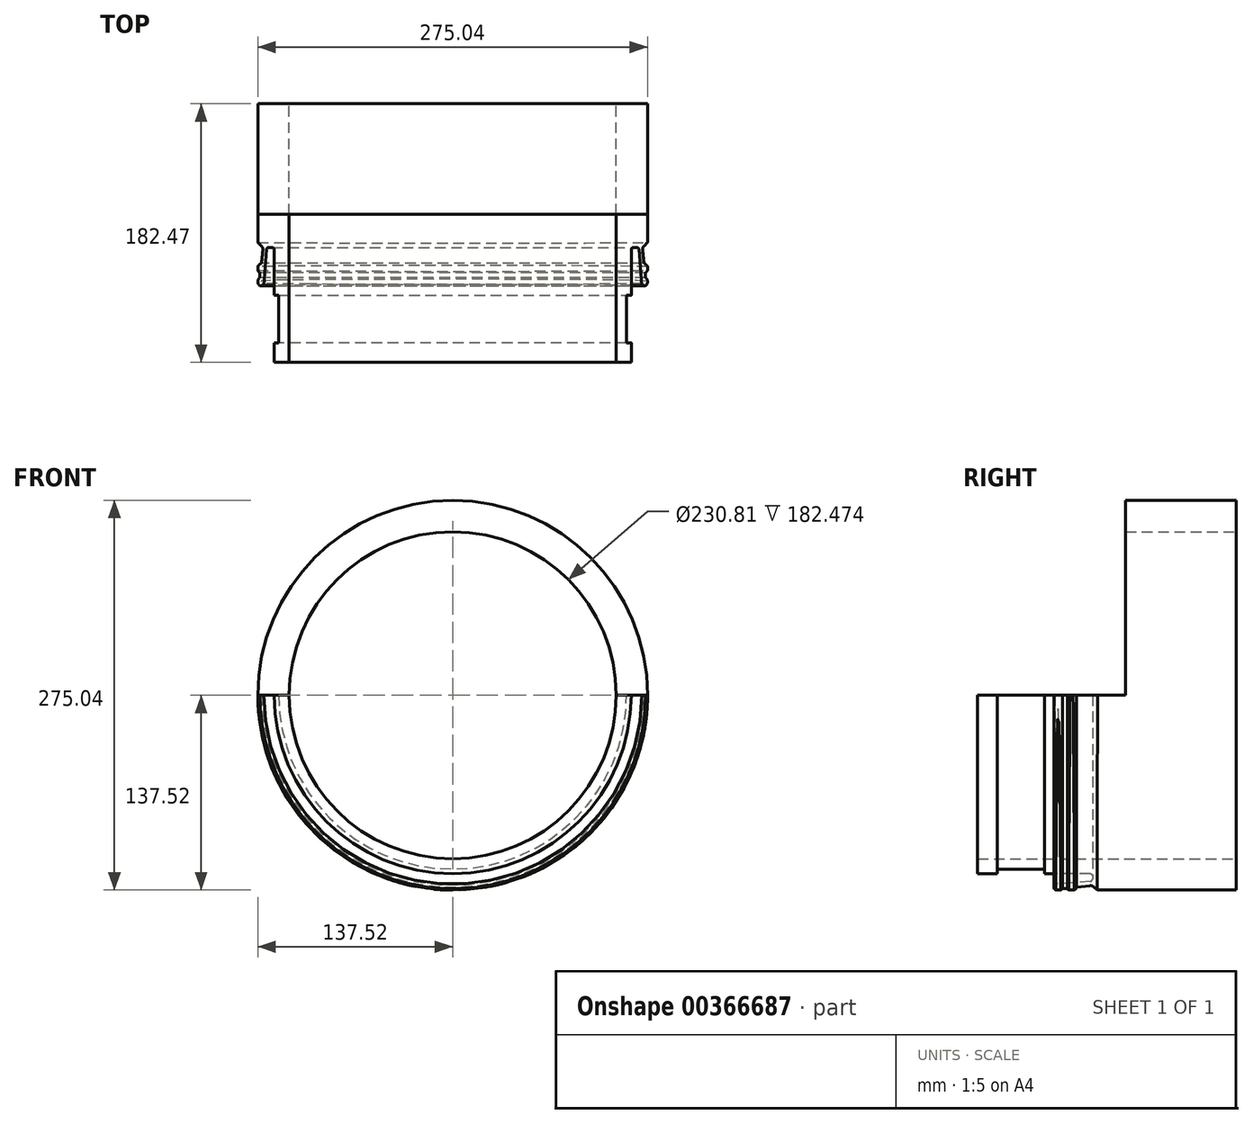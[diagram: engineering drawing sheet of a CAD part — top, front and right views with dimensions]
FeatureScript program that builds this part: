
annotation { "Feature Type Name" : "Feature", "Feature Type Description" : "" }
export const myFeature = defineFeature(function(context is Context, id is Id, definition is map)
    precondition{}
    {
        {
            var Q0;
            Q0=qCreatedBy(makeId("Front.planeOp"),FACE);
            var sketch = newSketch(context, id + "F0", { "sketchPlane" : qUnion([Q0])});
            skCircle(sketch, "E0", {"center": v(0, 0) * mm, "radius": 137.52 * mm});
            skCircle(sketch, "E1", {"center": v(0, 0) * mm, "radius": 115.4 * mm});
            skSolve(sketch);
        }
        {
            var Q0;
            Q0 = qSketchRegion(id + "F0", true);
            var Q1;
            Q1=makeQuery(id+"F0.imprint","IMPRINT",FACE,{"disambiguationData":[TD([[makeQuery(id+"F0.imprint","IMPRINT",EDGE,{"derivedFrom":sQuery(id+"F0.wireOp",EDGE,"E0")}),1.0]])]});
            extrude(context, id + "F1", {"entities" : qUnion([Q0, Q1]), "depth" : 182.47 * mm});
        }
        {
            var Q0;
            Q0=makeQuery(id+"F1.opExtrude","CAP_FACE",FACE,{"disambiguationData":[OSD([sQuery(id+"F0.wireOp",EDGE,"E0"),sQuery(id+"F0.wireOp",EDGE,"E1")])],"isStart":false});
            var sketch = newSketch(context, id + "F2", { "sketchPlane" : qUnion([Q0])});
            skCircle(sketch, "E2", {"center": v(0, 0) * mm, "radius": 125.98 * mm});
            skSolve(sketch);
        }
        {
            var Q0;
            Q0=makeQuery(id+"F2.imprint","IMPRINT",FACE,{"disambiguationData":[TD([[makeQuery(id+"F2.imprint","IMPRINT",EDGE,{"derivedFrom":makeQuery(id+"F1.opExtrude","CAP_EDGE",EDGE,{"disambiguationData":[OSD([sQuery(id+"F0.wireOp",EDGE,"E1")])],"isStart":false})}),1.0]])]});
            var Q1;
            Q1=makeQuery(id+"F2.imprint","IMPRINT",FACE,{"disambiguationData":[TD([[makeQuery(id+"F2.imprint","IMPRINT",EDGE,{"derivedFrom":sQuery(id+"F2.wireOp",EDGE,"E2")}),-1.0]])]});
            extrude(context, id + "F3", {"entities" : qUnion([Q0, Q1]), "operationType" : NewBodyOperationType.REMOVE, "oppositeDirection" : true, "depth" : 53.97 * mm});
        }
        {
            var Q0;
            Q0=qCreatedBy(makeId("Right.planeOp"),FACE);
            var sketch = newSketch(context, id + "F4", { "sketchPlane" : qUnion([Q0])});
            skLineSegment(sketch, "E3", {"start": v(0, 0) * mm, "end": v(-202.1, 0) * mm});
            skLineSegment(sketch, "E4", {"start": v(-182.47, 126.64) * mm, "end": v(-182.47, -30.08) * mm});
            skLineSegment(sketch, "E5", {"start": v(-135.23, 122.68) * mm, "end": v(-168.76, 122.68) * mm});
            skLineSegment(sketch, "E6", {"start": v(-135.23, 122.68) * mm, "end": v(-135.23, 133.6) * mm});
            skLineSegment(sketch, "E7", {"start": v(-168.76, 132.99) * mm, "end": v(-168.76, 122.68) * mm});
            skLineSegment(sketch, "E8", {"start": v(-168.76, 132.99) * mm, "end": v(-135.23, 133.6) * mm});
            skLineSegment(sketch, "E9", {"start": v(-128.5, 125.98) * mm, "end": v(-102.97, 125.98) * mm});
            skLineSegment(sketch, "E10", {"start": v(-101.45, 127.5) * mm, "end": v(-101.45, 129.88) * mm});
            skLineSegment(sketch, "E11", {"start": v(-128.5, 133.32) * mm, "end": v(-128.5, 125.98) * mm});
            skPoint(sketch, "E12", {"position": v(-128.5, 133.32) * mm});
            skLineSegment(sketch, "E13", {"start": v(-128.5, 133.32) * mm, "end": v(-102.86, 131.4) * mm});
            skArc(sketch, "E14.filletArc", {"start": v(-101.45, 129.88) * mm, "mid": v(-101.85, 130.91) * mm, "end": v(-102.86, 131.4) * mm});
            skPoint(sketch, "E15.visualSharp", {"position": v(-101.45, 125.98) * mm});
            skArc(sketch, "E15.filletArc", {"start": v(-102.97, 125.98) * mm, "mid": v(-101.9, 126.43) * mm, "end": v(-101.45, 127.5) * mm});
            skSolve(sketch);
        }
        {
            var Q0;
            Q0 = qSketchRegion(id + "F4", true);
            var Q1;
            Q1=sQuery(id+"F4.wireOp",EDGE,"E3");
            revolve(context, id + "F5", {"operationType" : NewBodyOperationType.REMOVE, "entities" : qUnion([Q0]), "axis" : qUnion([Q1]), "revolveType" : RevolveType.FULL, "oppositeDirection" : true});
        }
        {
            var Q0;
            Q0=qCreatedBy(makeId("Right.planeOp"),FACE);
            var sketch = newSketch(context, id + "F6", { "sketchPlane" : qUnion([Q0])});
            skLineSegment(sketch, "E16", {"start": v(-122.68, 135.64) * mm, "end": v(-119.23, 135.64) * mm});
            skLineSegment(sketch, "E17", {"start": v(-122.68, 135.64) * mm, "end": v(-122.68, 135.64) * mm});
            skArc(sketch, "E18.trimOffspring", {"start": v(-122.68, 135.64) * mm, "mid": v(-125.6, 137.03) * mm, "end": v(-128.5, 135.64) * mm});
            skPoint(sketch, "E19.start.orphan", {"position": v(-125.6, 137.03) * mm});
            skLineSegment(sketch, "E20", {"start": v(-128.5, 135.64) * mm, "end": v(-127.77, 131) * mm});
            skLineSegment(sketch, "E21", {"start": v(-116.2, 137.21) * mm, "end": v(-115.98, 137.21) * mm});
            skLineSegment(sketch, "E22", {"start": v(-115.98, 137.21) * mm, "end": v(-115.98, 137.2) * mm});
            skLineSegment(sketch, "E23", {"start": v(-112.65, 134.48) * mm, "end": v(-103.15, 133.48) * mm});
            skArc(sketch, "E24.trimOffspring", {"start": v(-112.65, 134.48) * mm, "mid": v(-115.57, 137.15) * mm, "end": v(-119.23, 135.64) * mm});
            skPoint(sketch, "E25.orphan", {"position": v(-97.38, 141.53) * mm});
            skPoint(sketch, "E26.orphan", {"position": v(-97.38, 138.2) * mm});
            skLineSegment(sketch, "E27", {"start": v(-97.38, 137.52) * mm, "end": v(-100.47, 134.43) * mm});
            skPoint(sketch, "E28.end.orphan", {"position": v(-97.38, 134.88) * mm});
            skPoint(sketch, "E29.visualSharp", {"position": v(-101.59, 133.31) * mm});
            skArc(sketch, "E30", {"start": v(-103.15, 133.48) * mm, "mid": v(-101.7, 133.65) * mm, "end": v(-100.47, 134.43) * mm});
            skLineSegment(sketch, "E31", {"start": v(-97.38, 137.52) * mm, "end": v(-97.38, 143.53) * mm});
            skLineSegment(sketch, "E32", {"start": v(-97.38, 143.53) * mm, "end": v(-140.06, 144.8) * mm});
            skLineSegment(sketch, "E33", {"start": v(-140.06, 144.8) * mm, "end": v(-134.24, 133.64) * mm});
            skLineSegment(sketch, "E34", {"start": v(-134.24, 133.64) * mm, "end": v(-127.77, 131) * mm});
            skLineSegment(sketch, "E35", {"start": v(1.03, -0.45) * mm, "end": v(-225.7, -0.45) * mm});
            skSolve(sketch);
        }
        {
            var Q0;
            Q0 = qSketchRegion(id + "F6", true);
            var Q1;
            Q1=sQuery(id+"F6.wireOp",EDGE,"E35");
            revolve(context, id + "F7", {"operationType" : NewBodyOperationType.REMOVE, "entities" : qUnion([Q0]), "axis" : qUnion([Q1]), "revolveType" : RevolveType.FULL});
        }
        {
            var Q0;
            Q0=makeQuery(id+"F1.opExtrude","CAP_FACE",FACE,{"disambiguationData":[OSD([sQuery(id+"F0.wireOp",EDGE,"E0"),sQuery(id+"F0.wireOp",EDGE,"E1")])],"isStart":false});
            var sketch = newSketch(context, id + "F8", { "sketchPlane" : qUnion([Q0])});
            skLineSegment(sketch, "E36", {"start": v(0, 0) * mm, "end": v(165.08, 0) * mm});
            skLineSegment(sketch, "E37", {"start": v(165.08, 0) * mm, "end": v(114.67, 125.2) * mm});
            skLineSegment(sketch, "E38", {"start": v(114.67, 125.2) * mm, "end": v(36.56, 149.57) * mm});
            skLineSegment(sketch, "E39", {"start": v(36.56, 149.57) * mm, "end": v(-42.65, 156.77) * mm});
            skLineSegment(sketch, "E40", {"start": v(-42.65, 156.77) * mm, "end": v(-131.84, 118) * mm});
            skLineSegment(sketch, "E41", {"start": v(-131.84, 118) * mm, "end": v(-156.22, 70.9) * mm});
            skLineSegment(sketch, "E42", {"start": v(-156.22, 70.9) * mm, "end": v(-171.17, 23.82) * mm});
            skLineSegment(sketch, "E43", {"start": v(-171.17, 23.82) * mm, "end": v(-171.17, 0) * mm});
            skLineSegment(sketch, "E44", {"start": v(-171.17, 0) * mm, "end": v(0, 0) * mm});
            skSolve(sketch);
        }
        {
            var Q0;
            Q0 = qSketchRegion(id + "F8", true);
            extrude(context, id + "F9", {"entities" : qUnion([Q0]), "operationType" : NewBodyOperationType.REMOVE, "oppositeDirection" : true, "depth" : 104.4 * mm});
        }
    });
